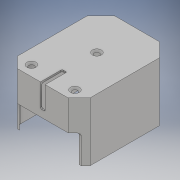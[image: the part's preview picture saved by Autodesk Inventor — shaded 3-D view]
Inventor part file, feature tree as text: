
AUTODESK INVENTOR PART (.ipt)
format: ipt  version: 2017 (Build 210142000, 142)  size: 447,488 bytes
history: native  units: mm
features: extrude x9, sketch x7, other x5, fillet x4, hole x3, projected_geometry x1
ambient origin geometry x8: Origin, YZ Plane, XZ Plane, XY Plane, X Axis, Y Axis, Z Axis, Center Point
bodies: Body1 (feature_tree)
feature tree (29):
  other  "Твердое тело1"
  sketch  "Эскиз1"
  extrude  "Выдавливание1"  Depth=58.6mm
  extrude  "Выдавливание2"  Depth=77.0mm
  fillet  "Сопряжение1"  Radius=11.0mm
  extrude  "Выдавливание3"  Depth=11.0mm
  extrude  "Выдавливание4"  Depth=8.5mm
  extrude  "Выдавливание5"  Depth=8.5mm
  other  "Комбинировать1"
  hole  "Отверстие4"  [1 undecoded]
  hole  "Отверстие5"  [1 undecoded]
  hole  "Отверстие6"  [1 undecoded]
  fillet  "Сопряжение2"  Radius=11.0mm
  fillet  "Сопряжение3"  Radius=1.2mm
  extrude  "Выдавливание6"  Depth=1.5mm TaperAngle=0.0deg
  extrude  "Выдавливание7"  Depth=48.0mm TaperAngle=0.0deg
  extrude  "Выдавливание8"  Depth=1.0mm
  other  "Комбинировать2"
  fillet  "Сопряжение4"  Radius=4.0mm
  extrude  "Выдавливание11"  Depth=17.0mm
  other  "Твердое тело2"
  sketch  "Эскиз2"
  sketch  "Эскиз3"
  sketch  "Эскиз4"
  other  "Твердое тело3"
  sketch  "Эскиз5"
  sketch  "Эскиз6"
  sketch  "Эскиз9"
  projected_geometry  "Спроецированная петля1"
note: 3 required parameter values undecoded (feature->parameter linkage not recoverable at this tier; creation-order binding heuristic only, values carry confidence <= 0.55)
